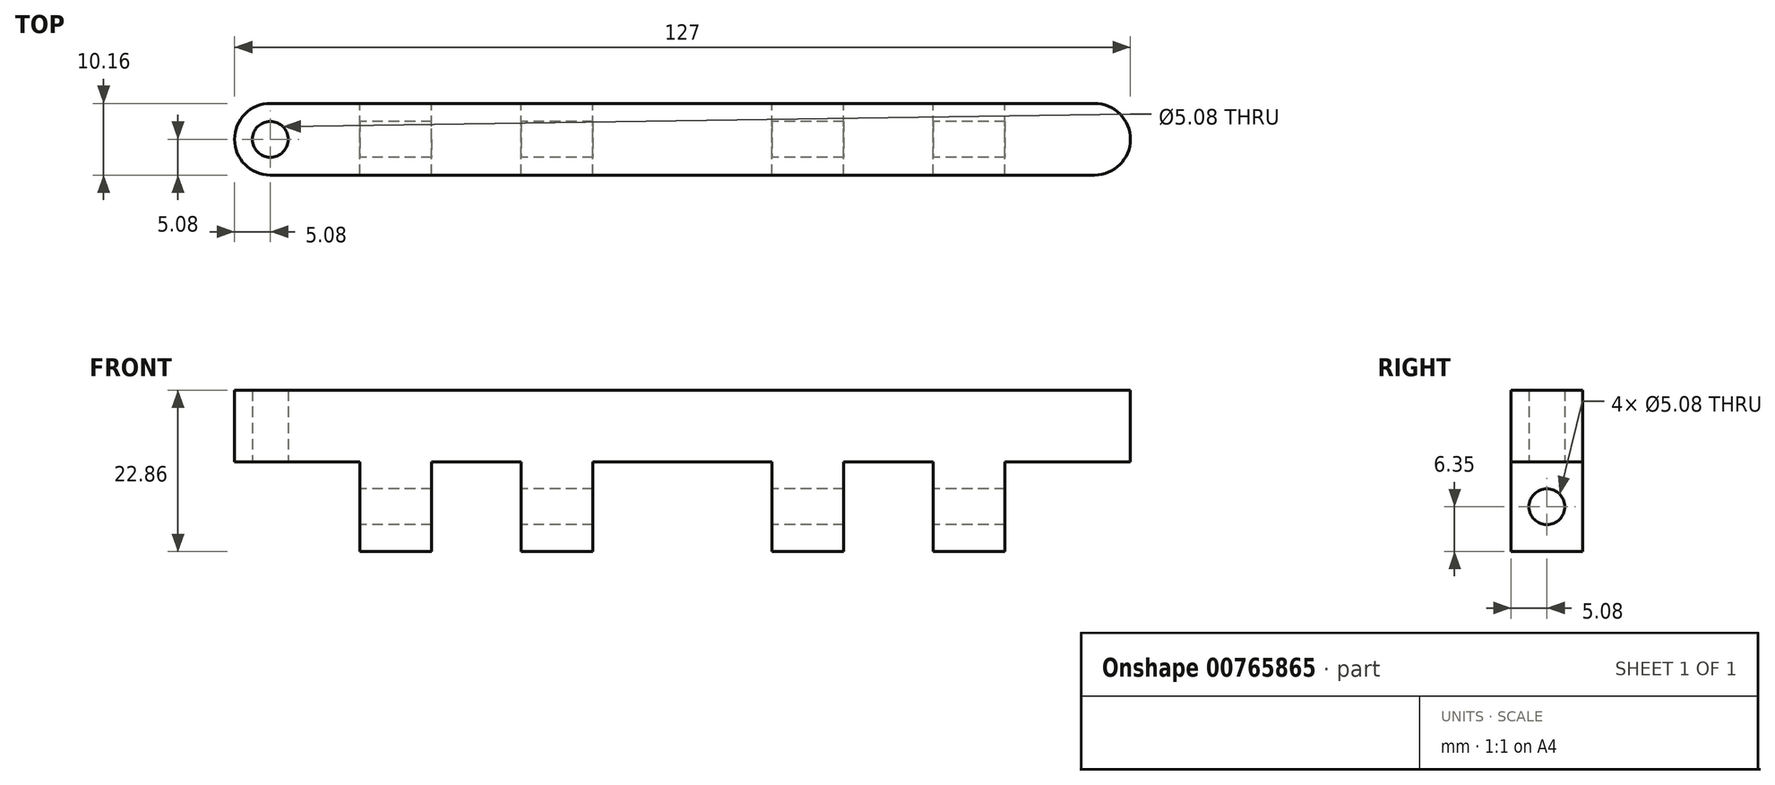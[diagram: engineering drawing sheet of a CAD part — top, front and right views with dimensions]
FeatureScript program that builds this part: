
annotation { "Feature Type Name" : "Feature", "Feature Type Description" : "" }
export const myFeature = defineFeature(function(context is Context, id is Id, definition is map)
    precondition{}
    {
        {
            var Q0;
            Q0=qCreatedBy(makeId("Top.planeOp"),FACE);
            var sketch = newSketch(context, id + "F0", { "sketchPlane" : qUnion([Q0])});
            skLineSegment(sketch, "E0.bottom", {"start": v(-63.5, -5.08) * mm, "end": v(63.5, -5.08) * mm});
            skLineSegment(sketch, "E0.top", {"start": v(-63.5, 5.08) * mm, "end": v(63.5, 5.08) * mm});
            skLineSegment(sketch, "E0.left", {"start": v(-63.5, -5.08) * mm, "end": v(-63.5, 5.08) * mm});
            skLineSegment(sketch, "E0.right", {"start": v(63.5, -5.08) * mm, "end": v(63.5, 5.08) * mm});
            skSolve(sketch);
        }
        {
            var Q0;
            Q0=makeQuery(id+"F0.imprint","IMPRINT",FACE,{"disambiguationData":[TD([[makeQuery(id+"F0.imprint","IMPRINT",EDGE,{"derivedFrom":sQuery(id+"F0.wireOp",EDGE,"E0.bottom")}),1.0]])]});
            extrude(context, id + "F1", {"entities" : qUnion([Q0]), "depth" : 10.16 * mm, "offsetDistance" : 25.4 * mm});
        }
        {
            var Q0;
            Q0=makeQuery(id+"F1.opExtrude","SWEPT_EDGE",EDGE,{"disambiguationData":[OSD([sQuery(id+"F0.wireOp",EDGE,"E0.bottom"),sQuery(id+"F0.wireOp",EDGE,"E0.left")])]});
            var Q1;
            Q1=makeQuery(id+"F1.opExtrude","SWEPT_EDGE",EDGE,{"disambiguationData":[OSD([sQuery(id+"F0.wireOp",EDGE,"E0.top"),sQuery(id+"F0.wireOp",EDGE,"E0.left")])]});
            var Q2;
            Q2=makeQuery(id+"F1.opExtrude","SWEPT_EDGE",EDGE,{"disambiguationData":[OSD([sQuery(id+"F0.wireOp",EDGE,"E0.bottom"),sQuery(id+"F0.wireOp",EDGE,"E0.right")])]});
            var Q3;
            Q3=makeQuery(id+"F1.opExtrude","SWEPT_EDGE",EDGE,{"disambiguationData":[OSD([sQuery(id+"F0.wireOp",EDGE,"E0.top"),sQuery(id+"F0.wireOp",EDGE,"E0.right")])]});
            fillet(context, id + "F2", {"entities" : qUnion([Q0, Q1, Q2, Q3]), "radius" : 5.08 * mm, "tangentPropagation" : true, "allowEdgeOverflow" : false});
        }
        {
            var Q0;
            Q0=makeQuery(id+"F1.opExtrude","CAP_FACE",FACE,{"disambiguationData":[OSD([sQuery(id+"F0.wireOp",EDGE,"E0.bottom"),sQuery(id+"F0.wireOp",EDGE,"E0.top"),sQuery(id+"F0.wireOp",EDGE,"E0.left"),sQuery(id+"F0.wireOp",EDGE,"E0.right")])],"isStart":true});
            var sketch = newSketch(context, id + "F3", { "sketchPlane" : qUnion([Q0])});
            skCircle(sketch, "E1", {"center": v(-58.42, 0) * mm, "radius": 2.54 * mm});
            skSolve(sketch);
        }
        {
            var Q0;
            Q0=makeQuery(id+"F3.imprint","IMPRINT",FACE,{"disambiguationData":[TD([[makeQuery(id+"F3.imprint","IMPRINT",EDGE,{"derivedFrom":sQuery(id+"F3.wireOp",EDGE,"E1")}),1.0]])]});
            extrude(context, id + "F4", {"entities" : qUnion([Q0]), "operationType" : NewBodyOperationType.REMOVE, "oppositeDirection" : true, "depth" : 25.4 * mm, "offsetDistance" : 25.4 * mm});
        }
        {
            var Q0;
            Q0=makeQuery(id+"F1.opExtrude","CAP_FACE",FACE,{"disambiguationData":[OSD([sQuery(id+"F0.wireOp",EDGE,"E0.bottom"),sQuery(id+"F0.wireOp",EDGE,"E0.top"),sQuery(id+"F0.wireOp",EDGE,"E0.left"),sQuery(id+"F0.wireOp",EDGE,"E0.right")])],"isStart":true});
            var sketch = newSketch(context, id + "F5", { "sketchPlane" : qUnion([Q0])});
            skLineSegment(sketch, "E2.bottom", {"start": v(-35.56, 5.08) * mm, "end": v(-45.72, 5.08) * mm});
            skLineSegment(sketch, "E2.top", {"start": v(-35.56, -5.08) * mm, "end": v(-45.72, -5.08) * mm});
            skLineSegment(sketch, "E2.left", {"start": v(-35.56, 5.08) * mm, "end": v(-35.56, -5.08) * mm});
            skLineSegment(sketch, "E2.right", {"start": v(-45.72, 5.08) * mm, "end": v(-45.72, -5.08) * mm});
            skPoint(sketch, "E2.middle", {"position": v(-40.64, 0) * mm});
            skLineSegment(sketch, "E3.bottom", {"start": v(-22.86, 5.08) * mm, "end": v(-12.7, 5.08) * mm});
            skLineSegment(sketch, "E3.top", {"start": v(-22.86, -5.08) * mm, "end": v(-12.7, -5.08) * mm});
            skLineSegment(sketch, "E3.left", {"start": v(-22.86, 5.08) * mm, "end": v(-22.86, -5.08) * mm});
            skLineSegment(sketch, "E3.right", {"start": v(-12.7, 5.08) * mm, "end": v(-12.7, -5.08) * mm});
            skPoint(sketch, "E3.middle", {"position": v(-17.78, 0) * mm});
            skLineSegment(sketch, "E4.MirrorCS", {"start": v(12.7, 5.08) * mm, "end": v(12.7, -5.08) * mm});
            skLineSegment(sketch, "E5.MirrorCS", {"start": v(22.86, -5.08) * mm, "end": v(12.7, -5.08) * mm});
            skLineSegment(sketch, "E6.MirrorCS", {"start": v(22.86, 5.08) * mm, "end": v(22.86, -5.08) * mm});
            skLineSegment(sketch, "E7.MirrorCS", {"start": v(22.86, 5.08) * mm, "end": v(12.7, 5.08) * mm});
            skLineSegment(sketch, "E8.MirrorCS", {"start": v(35.56, 5.08) * mm, "end": v(45.72, 5.08) * mm});
            skLineSegment(sketch, "E9.MirrorCS", {"start": v(45.72, 5.08) * mm, "end": v(45.72, -5.08) * mm});
            skLineSegment(sketch, "E10.MirrorCS", {"start": v(35.56, -5.08) * mm, "end": v(45.72, -5.08) * mm});
            skLineSegment(sketch, "E11.MirrorCS", {"start": v(35.56, 5.08) * mm, "end": v(35.56, -5.08) * mm});
            skSolve(sketch);
        }
        {
            var Q0;
            Q0 = qSketchRegion(id + "F5", true);
            extrude(context, id + "F6", {"entities" : qUnion([Q0]), "operationType" : NewBodyOperationType.ADD, "depth" : 12.7 * mm, "offsetDistance" : 25.4 * mm});
        }
        {
            var Q0;
            Q0=makeQuery(id+"F6.opExtrude","SWEPT_FACE",FACE,{"disambiguationData":[OSD([sQuery(id+"F5.wireOp",EDGE,"E2.right")])]});
            var sketch = newSketch(context, id + "F7", { "sketchPlane" : qUnion([Q0])});
            skCircle(sketch, "E12", {"center": v(0, -6.35) * mm, "radius": 2.54 * mm});
            skPoint(sketch, "E12.centerSnap0", {"position": v(5.08, -6.35) * mm});
            skSolve(sketch);
        }
        {
            var Q0;
            Q0=makeQuery(id+"F7.imprint","IMPRINT",FACE,{"disambiguationData":[TD([[makeQuery(id+"F7.imprint","IMPRINT",EDGE,{"derivedFrom":sQuery(id+"F7.wireOp",EDGE,"E12")}),1.0]])]});
            extrude(context, id + "F8", {"entities" : qUnion([Q0]), "operationType" : NewBodyOperationType.REMOVE, "oppositeDirection" : true, "depth" : 99.82 * mm, "offsetDistance" : 25.4 * mm});
        }
    });
